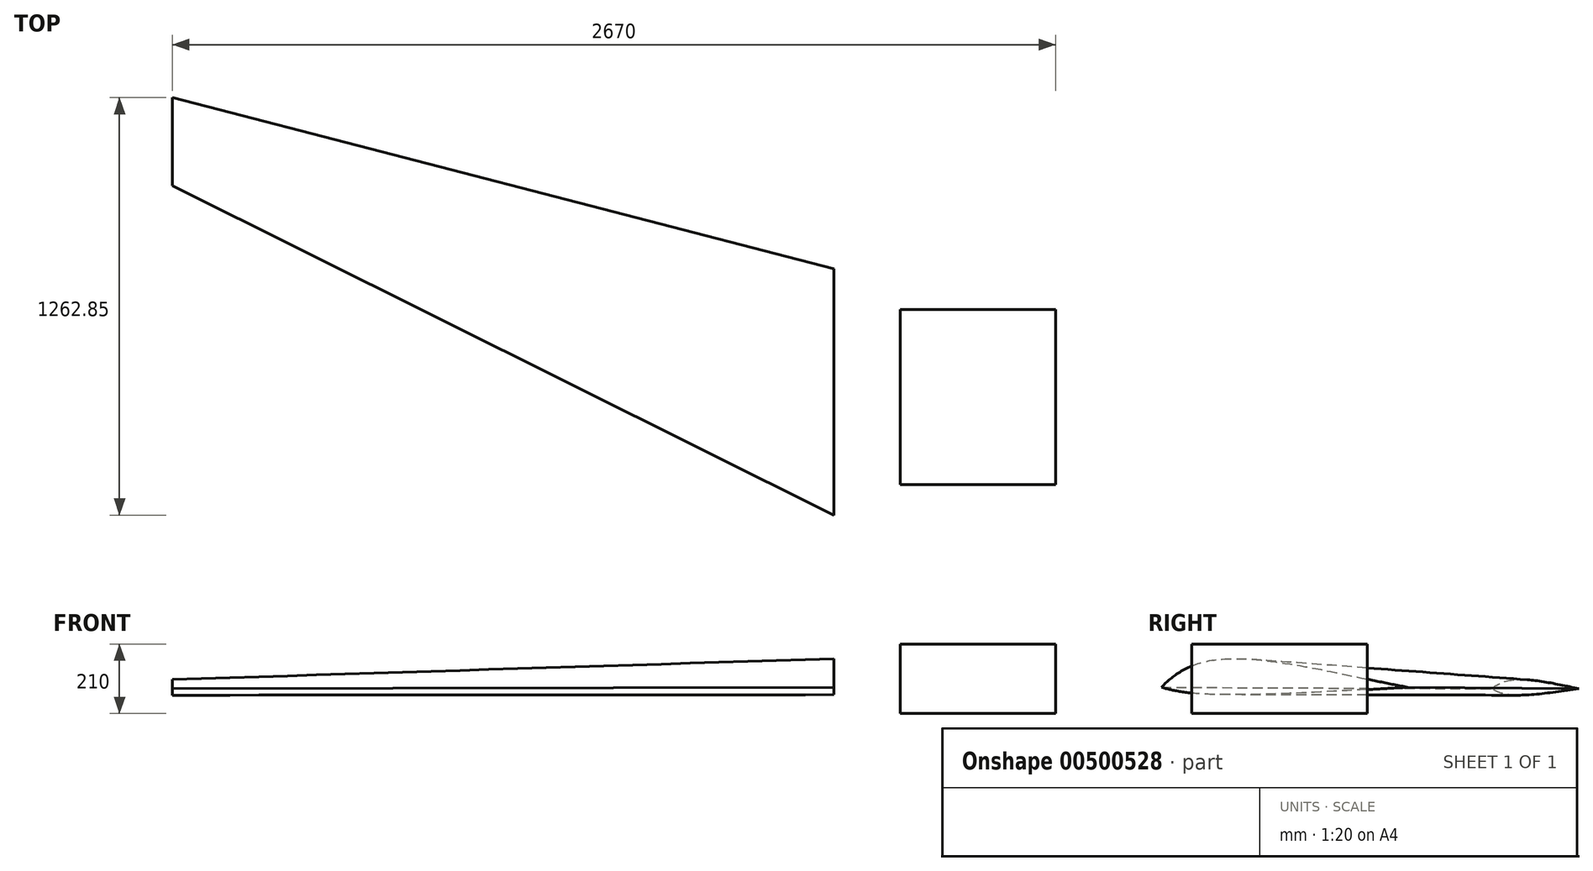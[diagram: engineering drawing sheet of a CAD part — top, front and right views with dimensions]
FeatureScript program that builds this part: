
annotation { "Feature Type Name" : "Feature", "Feature Type Description" : "" }
export const myFeature = defineFeature(function(context is Context, id is Id, definition is map)
    precondition{}
    {
        {
            var Q0;
            Q0=qCreatedBy(makeId("Top.planeOp"),FACE);
            var sketch = newSketch(context, id + "F0", { "sketchPlane" : qUnion([Q0])});
            skLineSegment(sketch, "E0.bottom", {"start": v(268.75, -265) * mm, "end": v(-201.25, -265) * mm});
            skLineSegment(sketch, "E0.top", {"start": v(268.75, 265) * mm, "end": v(-201.25, 265) * mm});
            skLineSegment(sketch, "E0.left", {"start": v(268.75, -265) * mm, "end": v(268.75, 265) * mm});
            skLineSegment(sketch, "E0.right", {"start": v(-201.25, -265) * mm, "end": v(-201.25, 265) * mm});
            skPoint(sketch, "E0.middle", {"position": v(33.75, 0) * mm});
            skSolve(sketch);
        }
        {
            var Q0;
            Q0 = qSketchRegion(id + "F0", true);
            extrude(context, id + "F1", {"entities" : qUnion([Q0]), "depth" : 210 * mm});
        }
        {
            var Q0;
            Q0=makeQuery(id+"F1.opExtrude","SWEPT_FACE",FACE,{"disambiguationData":[OSD([sQuery(id+"F0.wireOp",EDGE,"E0.right")])]});
            cPlane(context, id + "F2", {"entities" : qUnion([Q0]), "cplaneType" : CPlaneType.OFFSET, "offset" : 200 * mm, "width" : 150 * mm, "height" : 150 * mm});
        }
        {
            var Q0;
            Q0=qCreatedBy(id+"F2.planeOp",FACE);
            var sketch = newSketch(context, id + "F3", { "sketchPlane" : qUnion([Q0])});
            skFitSpline(sketch, "E1", {"points": [v(357.11, 78.93) * mm, v(212.82, 159.31) * mm, v(-387.66, 78.93) * mm], "startDerivative": vector(-219.69, 223.49) * mm, "endDerivative": vector(-920.92, -173.4) * mm});
            skFitSpline(sketch, "E2", {"points": [v(-387.66, 78.93) * mm, v(241.31, 59.11) * mm, v(357.11, 78.93) * mm], "startDerivative": vector(1081.22, -61.21) * mm, "endDerivative": vector(305.82, 79.86) * mm});
            skSolve(sketch);
        }
        {
            var Q0;
            Q0=qCreatedBy(id+"F2.planeOp",FACE);
            cPlane(context, id + "F4", {"entities" : qUnion([Q0]), "cplaneType" : CPlaneType.OFFSET, "offset" : 2000 * mm, "width" : 150 * mm, "height" : 150 * mm});
        }
        {
            var Q0;
            Q0=qCreatedBy(id+"F4.planeOp",FACE);
            var sketch = newSketch(context, id + "F5", { "sketchPlane" : qUnion([Q0])});
            skFitSpline(sketch, "E3", {"points": [v(-639.47, 74.55) * mm, v(-704.1, 101.26) * mm, v(-905.74, 74.55) * mm], "startDerivative": vector(-148.04, 93.46) * mm, "endDerivative": vector(-365.58, -78.51) * mm});
            skFitSpline(sketch, "E4", {"points": [v(-905.74, 74.55) * mm, v(-693.76, 56.45) * mm, v(-639.47, 74.55) * mm], "startDerivative": vector(375.57, -53.97) * mm, "endDerivative": vector(131.14, 66.73) * mm});
            skSolve(sketch);
        }
        {
            var Q0;
            Q0=makeQuery(id+"F3.imprint","IMPRINT",FACE,{"disambiguationData":[TD([[makeQuery(id+"F3.imprint","IMPRINT",EDGE,{"derivedFrom":sQuery(id+"F3.wireOp",EDGE,"E1")}),1.0]])]});
            var Q1;
            Q1=makeQuery(id+"F5.imprint","IMPRINT",FACE,{"disambiguationData":[TD([[makeQuery(id+"F5.imprint","IMPRINT",EDGE,{"derivedFrom":sQuery(id+"F5.wireOp",EDGE,"E3")}),1.0]])]});
            loft(context, id + "F6", {"sheetProfilesArray" : [{ "sheetProfileEntities" : qUnion([Q0]) }, { "sheetProfileEntities" : qUnion([Q1]) }]});
        }
    });
